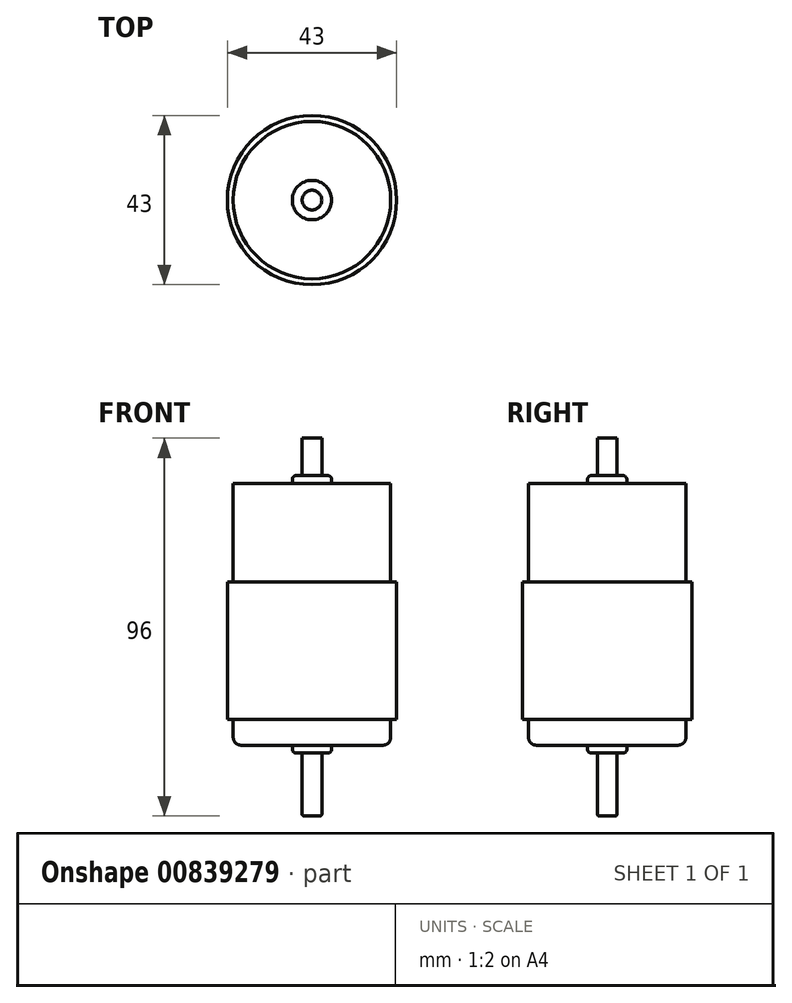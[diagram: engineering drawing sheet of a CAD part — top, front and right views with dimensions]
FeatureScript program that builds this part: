
annotation { "Feature Type Name" : "Feature", "Feature Type Description" : "" }
export const myFeature = defineFeature(function(context is Context, id is Id, definition is map)
    precondition{}
    {
        {
            var Q0;
            Q0=qCreatedBy(makeId("Top.planeOp"),FACE);
            var sketch = newSketch(context, id + "F0", { "sketchPlane" : qUnion([Q0])});
            skCircle(sketch, "E0", {"center": v(0, 0) * mm, "radius": 21.5 * mm});
            skSolve(sketch);
        }
        {
            var Q0;
            Q0=makeQuery(id+"F0.imprint","IMPRINT",FACE,{"disambiguationData":[TD([[makeQuery(id+"F0.imprint","IMPRINT",EDGE,{"derivedFrom":sQuery(id+"F0.wireOp",EDGE,"E0")}),1.0]])]});
            extrude(context, id + "F1", {"entities" : qUnion([Q0]), "oppositeDirection" : true, "depth" : 35 * mm, "offsetDistance" : 25 * mm});
        }
        {
            var Q0;
            Q0=makeQuery(id+"F1.opExtrude","CAP_FACE",FACE,{"disambiguationData":[OSD([sQuery(id+"F0.wireOp",EDGE,"E0")])],"isStart":true});
            var sketch = newSketch(context, id + "F2", { "sketchPlane" : qUnion([Q0])});
            skCircle(sketch, "E1", {"center": v(0, 0) * mm, "radius": 20 * mm});
            skSolve(sketch);
        }
        {
            var Q0;
            Q0=makeQuery(id+"F2.imprint","IMPRINT",FACE,{"disambiguationData":[TD([[makeQuery(id+"F2.imprint","IMPRINT",EDGE,{"derivedFrom":sQuery(id+"F2.wireOp",EDGE,"E1")}),1.0]])]});
            extrude(context, id + "F3", {"entities" : qUnion([Q0]), "operationType" : NewBodyOperationType.ADD, "depth" : 25 * mm, "offsetDistance" : 25 * mm});
        }
        {
            var Q0;
            Q0=makeQuery(id+"F3.opExtrude","CAP_FACE",FACE,{"disambiguationData":[OSD([sQuery(id+"F2.wireOp",EDGE,"E1")])],"isStart":false});
            var sketch = newSketch(context, id + "F4", { "sketchPlane" : qUnion([Q0])});
            skCircle(sketch, "E2", {"center": v(0, 0) * mm, "radius": 5 * mm});
            skSolve(sketch);
        }
        {
            var Q0;
            Q0=makeQuery(id+"F4.imprint","IMPRINT",FACE,{"disambiguationData":[TD([[makeQuery(id+"F4.imprint","IMPRINT",EDGE,{"derivedFrom":sQuery(id+"F4.wireOp",EDGE,"E2")}),1.0]])]});
            extrude(context, id + "F5", {"entities" : qUnion([Q0]), "operationType" : NewBodyOperationType.ADD, "depth" : 2 * mm, "offsetDistance" : 25 * mm});
        }
        {
            var Q0;
            Q0=makeQuery(id+"F1.opExtrude","CAP_FACE",FACE,{"disambiguationData":[OSD([sQuery(id+"F0.wireOp",EDGE,"E0")])],"isStart":false});
            var sketch = newSketch(context, id + "F6", { "sketchPlane" : qUnion([Q0])});
            skCircle(sketch, "E3", {"center": v(0, 0) * mm, "radius": 20 * mm});
            skSolve(sketch);
        }
        {
            var Q0;
            Q0=makeQuery(id+"F6.imprint","IMPRINT",FACE,{"disambiguationData":[TD([[makeQuery(id+"F6.imprint","IMPRINT",EDGE,{"derivedFrom":sQuery(id+"F6.wireOp",EDGE,"E3")}),1.0]])]});
            extrude(context, id + "F7", {"entities" : qUnion([Q0]), "operationType" : NewBodyOperationType.ADD, "depth" : 6.5 * mm, "offsetDistance" : 25 * mm});
        }
        {
            var Q0;
            Q0=makeQuery(id+"F7.opExtrude","CAP_EDGE",EDGE,{"disambiguationData":[OSD([sQuery(id+"F6.wireOp",EDGE,"E3")])],"isStart":false});
            fillet(context, id + "F8", {"entities" : qUnion([Q0]), "radius" : 2 * mm, "tangentPropagation" : true, "allowEdgeOverflow" : false});
        }
        {
            var Q0;
            Q0=makeQuery(id+"F7.opExtrude","CAP_FACE",FACE,{"disambiguationData":[OSD([sQuery(id+"F6.wireOp",EDGE,"E3")])],"isStart":false});
            var sketch = newSketch(context, id + "F9", { "sketchPlane" : qUnion([Q0])});
            skCircle(sketch, "E4", {"center": v(0, 0) * mm, "radius": 5 * mm});
            skSolve(sketch);
        }
        {
            var Q0;
            Q0=makeQuery(id+"F9.imprint","IMPRINT",FACE,{"disambiguationData":[TD([[makeQuery(id+"F9.imprint","IMPRINT",EDGE,{"derivedFrom":sQuery(id+"F9.wireOp",EDGE,"E4")}),1.0]])]});
            extrude(context, id + "F10", {"entities" : qUnion([Q0]), "operationType" : NewBodyOperationType.ADD, "depth" : 2 * mm, "offsetDistance" : 25 * mm});
        }
        {
            var Q0;
            Q0=makeQuery(id+"F10.opExtrude","CAP_EDGE",EDGE,{"disambiguationData":[OSD([sQuery(id+"F9.wireOp",EDGE,"E4")])],"isStart":false});
            fillet(context, id + "F11", {"entities" : qUnion([Q0]), "radius" : 1 * mm, "tangentPropagation" : true, "allowEdgeOverflow" : false});
        }
        {
            var Q0;
            Q0=makeQuery(id+"F10.opExtrude","CAP_FACE",FACE,{"disambiguationData":[OSD([sQuery(id+"F9.wireOp",EDGE,"E4")])],"isStart":false});
            var sketch = newSketch(context, id + "F12", { "sketchPlane" : qUnion([Q0])});
            skCircle(sketch, "E5", {"center": v(0, 0) * mm, "radius": 2.5 * mm});
            skSolve(sketch);
        }
        {
            var Q0;
            Q0=makeQuery(id+"F12.imprint","IMPRINT",FACE,{"disambiguationData":[TD([[makeQuery(id+"F12.imprint","IMPRINT",EDGE,{"derivedFrom":sQuery(id+"F12.wireOp",EDGE,"E5")}),1.0]])]});
            extrude(context, id + "F13", {"entities" : qUnion([Q0]), "operationType" : NewBodyOperationType.ADD, "depth" : 16 * mm, "offsetDistance" : 25 * mm});
        }
        {
            var Q0;
            Q0=makeQuery(id+"F13.opExtrude","CAP_EDGE",EDGE,{"disambiguationData":[OSD([sQuery(id+"F12.wireOp",EDGE,"E5")])],"isStart":false});
            fillet(context, id + "F14", {"entities" : qUnion([Q0]), "radius" : 0.5 * mm, "tangentPropagation" : true, "allowEdgeOverflow" : false});
        }
        {
            var Q0;
            Q0=makeQuery(id+"F5.opExtrude","CAP_EDGE",EDGE,{"disambiguationData":[OSD([sQuery(id+"F4.wireOp",EDGE,"E2")])],"isStart":false});
            fillet(context, id + "F15", {"entities" : qUnion([Q0]), "radius" : 1 * mm, "tangentPropagation" : true, "allowEdgeOverflow" : false});
        }
        {
            var Q0;
            Q0=makeQuery(id+"F5.opExtrude","CAP_FACE",FACE,{"disambiguationData":[OSD([sQuery(id+"F4.wireOp",EDGE,"E2")])],"isStart":false});
            var sketch = newSketch(context, id + "F16", { "sketchPlane" : qUnion([Q0])});
            skCircle(sketch, "E6", {"center": v(0, 0) * mm, "radius": 2.5 * mm});
            skSolve(sketch);
        }
        {
            var Q0;
            Q0=makeQuery(id+"F16.imprint","IMPRINT",FACE,{"disambiguationData":[TD([[makeQuery(id+"F16.imprint","IMPRINT",EDGE,{"derivedFrom":sQuery(id+"F16.wireOp",EDGE,"E6")}),1.0]])]});
            extrude(context, id + "F17", {"entities" : qUnion([Q0]), "operationType" : NewBodyOperationType.ADD, "depth" : 9.5 * mm, "offsetDistance" : 25 * mm});
        }
    });
